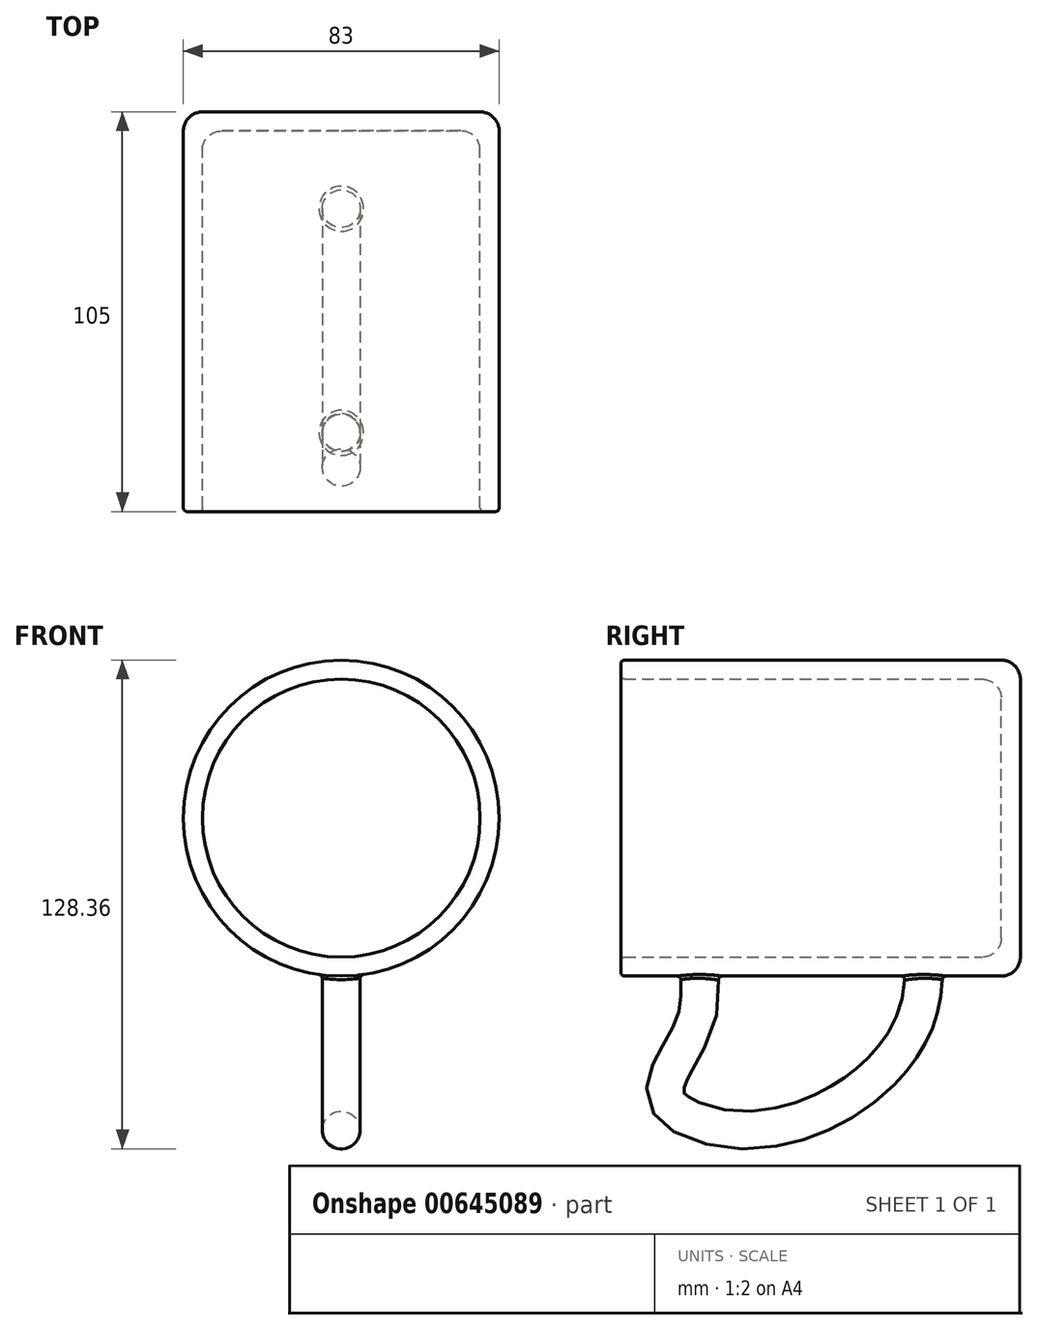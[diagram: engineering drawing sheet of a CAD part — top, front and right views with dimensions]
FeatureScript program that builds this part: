
annotation { "Feature Type Name" : "Feature", "Feature Type Description" : "" }
export const myFeature = defineFeature(function(context is Context, id is Id, definition is map)
    precondition{}
    {
        {
            var Q0;
            Q0=qCreatedBy(makeId("Front.planeOp"),FACE);
            var sketch = newSketch(context, id + "F0", { "sketchPlane" : qUnion([Q0])});
            skCircle(sketch, "E0", {"center": v(0, 0) * mm, "radius": 41.5 * mm});
            skSolve(sketch);
        }
        {
            var Q0;
            Q0 = qSketchRegion(id + "F0", true);
            extrude(context, id + "F1", {"entities" : qUnion([Q0]), "depth" : 105 * mm, "offsetDistance" : 25 * mm});
        }
        {
            var Q0;
            Q0=qCreatedBy(makeId("Right.planeOp"),FACE);
            var sketch = newSketch(context, id + "F2", { "sketchPlane" : qUnion([Q0])});
            skFitSpline(sketch, "E1", {"points": [v(-85.35, -32.2) * mm, v(-85.57, -54.77) * mm, v(-92.95, -72.66) * mm, v(-74.4, -81.6) * mm, v(-42.88, -71.54) * mm, v(-27.46, -51.87) * mm, v(-25.67, -33.1) * mm], "startDerivative": vector(22.76, -139.4) * mm, "endDerivative": vector(-3.13, 124.98) * mm});
            skSolve(sketch);
        }
        {
            var Q0;
            Q0=qCreatedBy(makeId("Top.planeOp"),FACE);
            cPlane(context, id + "F3", {"entities" : qUnion([Q0]), "cplaneType" : CPlaneType.OFFSET, "offset" : 32.9 * mm, "oppositeDirection" : true, "width" : 150 * mm, "height" : 150 * mm});
        }
        {
            var Q0;
            Q0=qCreatedBy(id+"F3.planeOp",FACE);
            var sketch = newSketch(context, id + "F4", { "sketchPlane" : qUnion([Q0])});
            skCircle(sketch, "E2", {"center": v(0, -85.51) * mm, "radius": 5 * mm});
            skSolve(sketch);
        }
        {
            var Q0;
            Q0 = qSketchRegion(id + "F4", true);
            extrude(context, id + "F5", {"entities" : qUnion([Q0]), "operationType" : NewBodyOperationType.ADD, "depth" : 25 * mm, "offsetDistance" : 25 * mm});
        }
        {
            var Q0;
            Q0 = qSketchRegion(id + "F4", true);
            var Q1;
            Q1=sQuery(id+"F2.wireOp",EDGE,"E1");
            sweep(context, id + "F6", {"operationType" : NewBodyOperationType.ADD, "profiles" : qUnion([Q0]), "path" : qUnion([Q1])});
        }
        {
            var Q0;
            Q0=makeQuery(id+"F1.opExtrude","CAP_FACE",FACE,{"disambiguationData":[OSD([sQuery(id+"F0.wireOp",EDGE,"E0")])],"isStart":false});
            shell(context, id + "F7", {"entities" : qUnion([Q0]), "thickness" : 5 * mm});
        }
        {
            var Q0;
            {var subQ0=sQuery(id+"F0.wireOp",EDGE,"E0");Q0=makeQuery(id+"F7.opShell","OFFSET_EDGE",EDGE,{"disambiguationData":[OSD([subQ0]),TDD([makeQuery(id+"F1.opExtrude","CAP_EDGE",EDGE,{"disambiguationData":[OSD([subQ0])],"isStart":false})])]});}
            var Q1;
            Q1=makeQuery(id+"F1.opExtrude","CAP_EDGE",EDGE,{"disambiguationData":[OSD([sQuery(id+"F0.wireOp",EDGE,"E0")])],"isStart":false});
            var Q2;
            Q2=makeQuery(id+"F6.boolean.opBoolean","INTERSECT",EDGE,{"disambiguationData":[OD(0.0)],"derivedFrom":[makeQuery(id+"F1.opExtrude","SWEPT_FACE",FACE,{"disambiguationData":[OSD([sQuery(id+"F0.wireOp",EDGE,"E0")])]}),makeQuery(id+"F6.opSweep","SWEPT_FACE",FACE,{"disambiguationData":[OSD([sQuery(id+"F2.wireOp",EDGE,"E1"),sQuery(id+"F4.wireOp",EDGE,"E2")])]})]});
            var Q3;
            Q3=makeQuery(id+"F6.boolean.opBoolean","INTERSECT",EDGE,{"disambiguationData":[OD(1.0)],"derivedFrom":[makeQuery(id+"F1.opExtrude","SWEPT_FACE",FACE,{"disambiguationData":[OSD([sQuery(id+"F0.wireOp",EDGE,"E0")])]}),makeQuery(id+"F6.opSweep","SWEPT_FACE",FACE,{"disambiguationData":[OSD([sQuery(id+"F2.wireOp",EDGE,"E1"),sQuery(id+"F4.wireOp",EDGE,"E2")])]})]});
            fillet(context, id + "F8", {"entities" : qUnion([Q0, Q1, Q2, Q3]), "radius" : 1 * mm, "tangentPropagation" : true, "allowEdgeOverflow" : false});
        }
        {
            var Q0;
            Q0=makeQuery(id+"F1.opExtrude","CAP_EDGE",EDGE,{"disambiguationData":[OSD([sQuery(id+"F0.wireOp",EDGE,"E0")])],"isStart":true});
            fillet(context, id + "F9", {"entities" : qUnion([Q0]), "radius" : 5 * mm, "tangentPropagation" : true, "allowEdgeOverflow" : false});
        }
        {
            var Q0;
            {var subQ0=sQuery(id+"F0.wireOp",EDGE,"E0");Q0=makeQuery(id+"F7.opShell","OFFSET_EDGE",EDGE,{"disambiguationData":[OSD([subQ0]),TDD([makeQuery(id+"F1.opExtrude","CAP_EDGE",EDGE,{"disambiguationData":[OSD([subQ0])],"isStart":true})])]});}
            fillet(context, id + "F10", {"entities" : qUnion([Q0]), "radius" : 5 * mm, "tangentPropagation" : true, "allowEdgeOverflow" : false});
        }
    });
